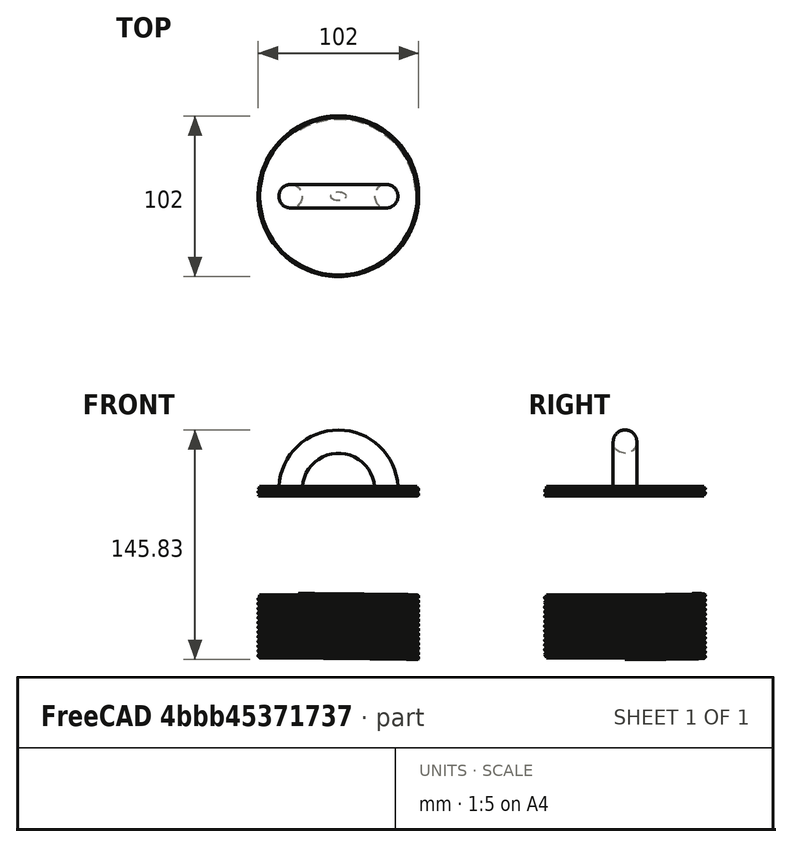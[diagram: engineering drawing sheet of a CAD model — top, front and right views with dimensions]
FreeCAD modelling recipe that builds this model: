
FCSTD DOCUMENT  (FreeCAD 0.17R13522 (Git))
Label: tuna_wringer_top
License: CreativeCommons Attribution-ShareAlike
LicenseURL: http://creativecommons.org/licenses/by-sa/4.0/
objects: Part::Cut×22, Part::Feature×16, Part::Cylinder×10, Part::MultiFuse×5, Sketcher::SketchObject×3, Part::Extrusion×3, Part::Box×3, Part::Sweep×2, Part::Helix×1, PartDesign::ShapeBinder×1, PartDesign::Body×1, Part::Ellipse×1, Part::FeaturePython×1, Part::MultiCommon×1, App::DocumentObjectGroup×1
note: 70 computed .brp shape members not serialized (recipe doc carries the construction recipe); baked Part::Feature solids carry a one-line shape summary decoded from their .brp

FEATURE [Part::Cylinder] Cylinder
  Angle = 360
  AttacherType = Attacher::AttachEngine3D
  Height = 40
  Radius = 50
FEATURE [Part::Helix] Helix
  Angle = 0
  AttacherType = Attacher::AttachEngine3D
  Height = 40
  LocalCoord = 0
  Pitch = 3
  Radius = 50
  Style = 1
FEATURE [Sketcher::SketchObject] Sketch
  MapMode = 5
  Placement = pos=(0,0,0) rot=(1,0,0;1.5708rad)
  Support = -> [XZ_Plane]
  sketch-geometry (1):
    g0: Circle CenterX=50 CenterY=0 CenterZ=0 NormalX=0 NormalY=0 NormalZ=1 AngleXU=0 Radius=1
  constraints (3):
    c: PointOnObject(g0,g-1)
    c: Radius(g0) = 1
    c: DistanceX(g-1,g0) = 50
FEATURE [Part::Sweep] Sweep
  Frenet = false
  Sections = -> [Sketch]
  Solid = true
  Spine = -> Helix
  Transition = 1
FEATURE [Part::MultiFuse] Fusion  label="base_roscada_media"
  Shapes = -> [Sweep,Cylinder]
FEATURE [Part::Cylinder] Cylinder001  label="base_parte_inferior"
  Angle = 360
  AttacherType = Attacher::AttachEngine3D
  Height = 35
  Placement = pos=(0,0,-30) rot=(0,0,1;0rad)
  Radius = 52
FEATURE [Part::Feature] Fusion001  label="base_roscada_media_para_roscar_recipiente_inferior"
  shape: bbox 110.9 x 119.3 x 43.76 mm, 46 faces (baked)
FEATURE [Part::Cut] Cut
  Base = -> Cylinder001
  Tool = -> Fusion001
FEATURE [Part::Cylinder] Cylinder002  label="perforador_parte_inferior"
  Angle = 360
  AttacherType = Attacher::AttachEngine3D
  Height = 29
  Placement = pos=(0,0,-28) rot=(0,0,1;0rad)
  Radius = 49
FEATURE [Part::Cut] Cut001  label="parte_inferior_done"
  Base = -> Cut
  Placement = pos=(0,0,-66) rot=(0,0,1;0rad)
  Tool = -> Cylinder002
FEATURE [Part::Feature] Fusion002  label="base_roscada_media001"
  shape: bbox 110.9 x 119.3 x 43.76 mm, 46 faces (baked)
FEATURE [Part::Cylinder] Cylinder003  label="Cylinder001"
  Angle = 360
  AttacherType = Attacher::AttachEngine3D
  Height = 40
  Placement = pos=(0,0,5) rot=(0,0,1;0rad)
  Radius = 52
FEATURE [Part::MultiFuse] Fusion003  label="parte_media_comienzo"
  Shapes = -> [Fusion002,Cylinder003]
FEATURE [Part::Feature] Fusion004  label="base_roscada_media002"
  Placement = pos=(0,0,8) rot=(0,0,1;0rad)
  shape: bbox 110.9 x 119.3 x 43.76 mm, 46 faces (baked)
FEATURE [Part::Cut] Cut002  label="parte_media_2"
  Base = -> Fusion003
  Tool = -> Fusion004
FEATURE [Part::Cylinder] Cylinder004  label="Cylinder002"
  Angle = 360
  AttacherType = Attacher::AttachEngine3D
  Height = 10
  Placement = pos=(0,0,-10) rot=(0,0,1;0rad)
  Radius = 60
FEATURE [Part::Cut] Cut003  label="parte_media_sin_perforar"
  Base = -> Cut002
  Tool = -> Cylinder004
FEATURE [Part::Feature] Fusion005  label="tapa_rosca"
  shape: bbox 110.9 x 119.3 x 43.76 mm, 46 faces (baked)
FEATURE [Part::Cylinder] Cylinder005  label="Cylinder003"
  Angle = 360
  AttacherType = Attacher::AttachEngine3D
  Height = 40
  Placement = pos=(0,0,4) rot=(0,0,1;0rad)
  Radius = 54
FEATURE [Part::Cut] Cut004
  Base = -> Fusion005
  Tool = -> Cylinder005
FEATURE [Part::Cylinder] Cylinder006  label="Cylinder004"
  Angle = 360
  AttacherType = Attacher::AttachEngine3D
  Height = 1
  Placement = pos=(0,0,4) rot=(0,0,1;0rad)
  Radius = 50
FEATURE [Part::MultiFuse] Fusion006
  Shapes = -> [Cut004,Cylinder006]
FEATURE [PartDesign::ShapeBinder] CopyFusion006
  Placement = pos=(0,0,4) rot=(0,0,1;0rad)
FEATURE [PartDesign::Body] Body
  Group = -> [Sketch,CopyFusion006]
  Origin = -> Origin
FEATURE [Sketcher::SketchObject] Sketch001
  Placement = pos=(0,0,0) rot=(1,0,0;1.5708rad)
  sketch-geometry (1):
    g0: ArcOfCircle CenterX=0 CenterY=0 CenterZ=0 NormalX=0 NormalY=0 NormalZ=1 AngleXU=0 Radius=30.8415 StartAngle=0.00522177 EndAngle=3.12837
  constraints (1):
    c: Coincident(g0,g-1)
FEATURE [Sketcher::SketchObject] Sketch002
  Placement = pos=(0,0,5) rot=(0,0,1;0rad)
  sketch-geometry (1):
    g0: Circle CenterX=30 CenterY=0 CenterZ=0 NormalX=0 NormalY=0 NormalZ=1 AngleXU=0 Radius=7.5
  constraints (3):
    c: PointOnObject(g0,g-1)
    c: Radius(g0) = 7.5
    c: DistanceX(g-1,g0) = 30
FEATURE [Part::Sweep] Sweep001  label="manija"
  Frenet = false
  Placement = pos=(0,0,3) rot=(0,0,1;0rad)
  Sections = -> [Sketch002]
  Solid = true
  Spine = -> Sketch001
  Transition = 1
FEATURE [Part::MultiFuse] Fusion007  label="tapa_con_rosca"
  Placement = pos=(0,0,104) rot=(0,0,1;0rad)
  Shapes = -> [Fusion006,Sweep001]
FEATURE [Part::Ellipse] Ellipse
  Angle0 = 0
  Angle1 = 360
  AttacherType = Attacher::AttachEngine3D
  MajorRadius = 5
  MinorRadius = 2.5
FEATURE [Part::Extrusion] Extrude
  Base = -> Ellipse
  Dir = (0,0,1)
  DirMode = 2
  FaceMakerClass = Part::FaceMakerBullseye
  LengthFwd = 20
  LengthRev = 0
  Solid = true
  Symmetric = false
FEATURE [Part::Extrusion] Extrude001
  Base = -> Ellipse
  Dir = (0,0,1)
  DirMode = 2
  FaceMakerClass = Part::FaceMakerBullseye
  LengthFwd = 20
  LengthRev = 0
  Solid = true
  Symmetric = false
FEATURE [Part::Extrusion] Extrude002
  Base = -> Ellipse
  Dir = (0,0,1)
  DirMode = 2
  FaceMakerClass = Part::FaceMakerBullseye
  LengthFwd = 20
  LengthRev = 0
  Solid = true
  Symmetric = false
FEATURE [Part::FeaturePython] Array  # Draft array (typed FeaturePython)
  Angle = 360
  ArrayType = 0
  Axis = (0,0,1)
  Base = -> Extrude
  Center = (0,0,0)
  Fuse = false
  IntervalAxis = (0,0,0)
  IntervalX = (14,0,0)
  IntervalY = (0,9,0)
  IntervalZ = (0,0,0)
  NumberPolar = 1
  NumberX = 30
  NumberY = 30
  NumberZ = 1
FEATURE [Part::Cylinder] Cylinder007  label="Cylinder005"
  Angle = 360
  AttacherType = Attacher::AttachEngine3D
  Height = 50
  Placement = pos=(77,135,-2) rot=(0,0,1;0rad)
  Radius = 48
FEATURE [Part::MultiCommon] Common
  Placement = pos=(39,-136,0) rot=(0,0,1;0rad)
  Shapes = -> [Array,Cylinder007]
FEATURE [Part::Box] Box  label="Cube"
  AttacherType = Attacher::AttachEngine3D
  Height = 60
  Length = 10
  Placement = pos=(92,40,-5) rot=(0,0,1;0rad)
  Width = 10
FEATURE [Part::Feature] Box001  label="Cube001"
  Placement = pos=(132,40,-5) rot=(0,0,1;0rad)
  shape: bbox 10 x 10 x 60 mm, 6 faces (baked)
FEATURE [Part::Feature] Box001001  label="Cube002"
  Placement = pos=(146,30,-5) rot=(0,0,1;0rad)
  shape: bbox 10 x 10 x 60 mm, 6 faces (baked)
FEATURE [Part::Feature] Box001001001  label="Cube003"
  Placement = pos=(77,30,-5) rot=(0,0,1;0rad)
  shape: bbox 10 x 10 x 60 mm, 6 faces (baked)
FEATURE [Part::Feature] Box001001001001  label="Cube004"
  Placement = pos=(77,-43,-5) rot=(0,0,1;0rad)
  shape: bbox 10 x 10 x 60 mm, 6 faces (baked)
FEATURE [Part::Feature] Box001001001001001  label="Cube005"
  Placement = pos=(146,-43,-5) rot=(0,0,1;0rad)
  shape: bbox 10 x 10 x 60 mm, 6 faces (baked)
FEATURE [Part::Feature] Box001001001001001001  label="Cube006"
  Placement = pos=(130,-52,-5) rot=(0,0,1;0rad)
  shape: bbox 10 x 10 x 60 mm, 6 faces (baked)
FEATURE [Part::Feature] Box001001001001001001001  label="Cube007"
  Placement = pos=(91,-52,-5) rot=(0,0,1;0rad)
  shape: bbox 10 x 10 x 60 mm, 6 faces (baked)
FEATURE [Part::Feature] Box001001001001001001002  label="Cube008"
  Placement = pos=(64,13,-5) rot=(0,0,1;0rad)
  shape: bbox 10 x 10 x 60 mm, 6 faces (baked)
FEATURE [Part::Feature] Box001001001001001001002001  label="Cube009"
  Placement = pos=(64,-25,-5) rot=(0,0,1;0rad)
  shape: bbox 10 x 10 x 60 mm, 6 faces (baked)
FEATURE [Part::Feature] Box001001001001001001002001001  label="Cube010"
  Placement = pos=(159,-25,-5) rot=(0,0,1;0rad)
  shape: bbox 10 x 10 x 60 mm, 6 faces (baked)
FEATURE [Part::Feature] Box001001001001001001002001001001  label="Cube011"
  Placement = pos=(159,12,-5) rot=(0,0,1;0rad)
  shape: bbox 10 x 10 x 60 mm, 6 faces (baked)
FEATURE [Part::Cut] Cut005
  Base = -> Common
  Tool = -> Box
FEATURE [Part::Cut] Cut006
  Base = -> Cut005
  Tool = -> Box001
FEATURE [Part::Cut] Cut007
  Base = -> Cut006
  Tool = -> Box001001
FEATURE [Part::Cut] Cut008
  Base = -> Cut007
  Tool = -> Box001001001
FEATURE [Part::Cut] Cut009
  Base = -> Cut008
  Tool = -> Box001001001001
FEATURE [Part::Cut] Cut010
  Base = -> Cut009
  Tool = -> Box001001001001001
FEATURE [Part::Cut] Cut011
  Base = -> Cut010
  Tool = -> Box001001001001001001
FEATURE [Part::Cut] Cut012
  Base = -> Cut011
  Tool = -> Box001001001001001001001
FEATURE [Part::Cut] Cut013
  Base = -> Cut012
  Tool = -> Box001001001001001001002
FEATURE [Part::Cut] Cut014
  Base = -> Cut013
  Tool = -> Box001001001001001001002001
FEATURE [Part::Cut] Cut015
  Base = -> Cut014
  Tool = -> Box001001001001001001002001001
FEATURE [Part::Cut] Cut016  label="rejilla"
  Base = -> Cut015
  Placement = pos=(-116,1,-9) rot=(0,0,1;0rad)
  Tool = -> Box001001001001001001002001001001
FEATURE [Part::Cut] Cut017  label="parte_media"
  Base = -> Cut003
  Tool = -> Cut016
FEATURE [Part::Box] Box001001001001001001002001001002  label="Cube012"
  AttacherType = Attacher::AttachEngine3D
  Height = 165
  Length = 120
  Placement = pos=(-60,-58,-112) rot=(0,0,1;0rad)
  Width = 120
FEATURE [Part::Box] Box001001001001001001002001001003  label="Cube013"
  AttacherType = Attacher::AttachEngine3D
  Height = 165
  Length = 120
  Placement = pos=(-60,-58,-112) rot=(0,0,1;0rad)
  Width = 120
FEATURE [Part::Cut] Cut018
  Base = -> Cut017
  Tool = -> Box001001001001001001002001001002
FEATURE [Part::Cut] Cut019
  Base = -> Cut001
  Tool = -> Box001001001001001001002001001003
FEATURE [App::DocumentObjectGroup] Group  label="not used"
  Group = -> [Extrude001,Extrude002,Cut018,Cut019,Helix,Body,Fusion,Sketch001]
FEATURE [Part::Cylinder] Cylinder008  label="Cylinder006"
  Angle = 360
  AttacherType = Attacher::AttachEngine3D
  Height = 10
  Placement = pos=(0,0,98) rot=(0,0,1;0rad)
  Radius = 60
FEATURE [Part::Cut] Cut020  label="tapa_sin_rosca"
  Base = -> Fusion007
  Tool = -> Cylinder008
FEATURE [Part::Feature] Cut022001  label="Cut023"
  Placement = pos=(0,0,-55) rot=(0,0,1;0rad)
  shape: bbox 108.9 x 117.3 x 43.86 mm, 42 faces (baked)
FEATURE [Part::Cylinder] Cylinder009  label="Cylinder007"
  Angle = 360
  AttacherType = Attacher::AttachEngine3D
  Height = 50
  Placement = pos=(0,0,-45) rot=(0,0,1;0rad)
  Radius = 60
FEATURE [Part::Cut] Cut022002
  Base = -> Cut022001
  Placement = pos=(0,0,153) rot=(0,0,1;0rad)
  Tool = -> Cylinder009
FEATURE [Part::MultiFuse] Fusion008  label="tapa_con_rosca_098"
  Shapes = -> [Cut020,Cut022002]
